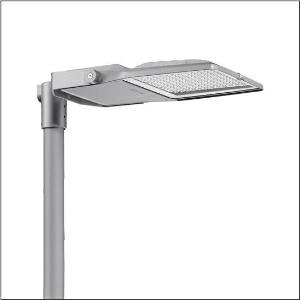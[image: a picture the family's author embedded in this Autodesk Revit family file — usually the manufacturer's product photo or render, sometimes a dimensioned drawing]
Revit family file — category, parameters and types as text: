
# Revit family: floodlight_fl_21_midi___pl64_5xa7785f2e3a_d9f8
name_source: partatom
category: Lighting Fixtures
units: mm (PartAtom-declared; Revit-internal decimal feet)

## family parameters
Cut with Voids When Loaded = No
Host = Face
Light Source = No
Part Type = Normal
Room Calculation Point = No
Round Connector Dimension = Use Diameter
Shared = No

## types (1)
- --- (1 x LED, 34530 lm, 271.6 W, 3000K)
    Apparent Load = 272 VA
    CIE Flux Codes = 28 80 98 100 100
    Color Rendering = 70
    Color Temperature = 3000K
    Default Elevation = 1800 mm
    Description = Floodlight FL 21 midi, floodlight, primary light control with lens, of PMMA, primary optical cover: protective disc, of toughened safety glass, transparent, light distribution: PL64, light emission: direct distribution, installation type: surface-mounted, LED, High Power LED, rated luminous flux: 34.530lm, luminous efficacy: 127lm/W, light colour: 730, colour temperature: 3000K, control gear: ECG Smart Interface, control: flexible luminous flux parameterisation, time-dependent luminous flux control, constant luminous flux control, overheat protection, presetting dimming logarithmic, with terminal, 6-pole, mains connection: 220..240V, AC, 50/60Hz, start of lifetime: 272W, end of service life: 287W, reduction: 123W, luminaire housing, of diecast aluminium, powder-coated, Siteco® metallic grey (DB 702S), sealing non-destructively replaceable, please order mast flange separately, mast bracket, of steel, galvanised, powder-coated, Siteco® metallic grey (DB 702S), Smart Interface above, protection rating (complete): IP66, insulation class (complete): insulation class II (safety insulation), certification: CE, protection symbol: D, impact resistance: IK08, permissible operating ambient temperature: -40..+40°C, permissible operating ambient temperature for outdoor applications: -40..+50°C, standard: DIN EN 12944, LABS conformity tested according to VDMA 24364:2018-05, packaging unit: 1 piece

Light Distribution: PL64
    Height = 76 mm
    Lamp = 1 x LED
    Lamp Light Flux = 34530 lm
    Lamp Power = 271.6 W
    Lamp count = 1
    Length = 657 mm
    Luminous efficacy = 127 lm/W
    Manufacturer = Siteco
    ModVariant = No
    Model = 5XA7785F2E3A
    Number of Poles = 1
    OnlyDefault = Yes
    Power Factor = 1
    Product Name = Floodlight FL 21 midi | PL64
    Product group = floodlight | pylon annexe
    ProductGroupID = 6200
    Protection Class = Protection class II
    Protection Degree = IP 66
    RLX_Detail_Level = 1
    RLX_Emergency_Light_Flux = 0 lm
    RLX_Emergency_Type = 0
    RLX_Emergency_Type_DB = No
    RlxData = <blob elided: 153493 chars, md5=da029b77>
    Socket = socket
    Standby Power = 0 W
    System Light Flux = 34530 lm
    System Power = 272 W
    Type Comments = factory setting: luminous flux: 100 % | dim-lin: 254 | 620 mA
    Type Image = l_1007123.jpg
    URL = http://relux.com
    VarID = @adj_131679
    Voltage = 0 V
    Weight = 0.00 kg
    Width = 442 mm

## geometry (parser evidence)
native form markers: Blend x4, Sweep x17
no freeform markers — native parametric forms only
